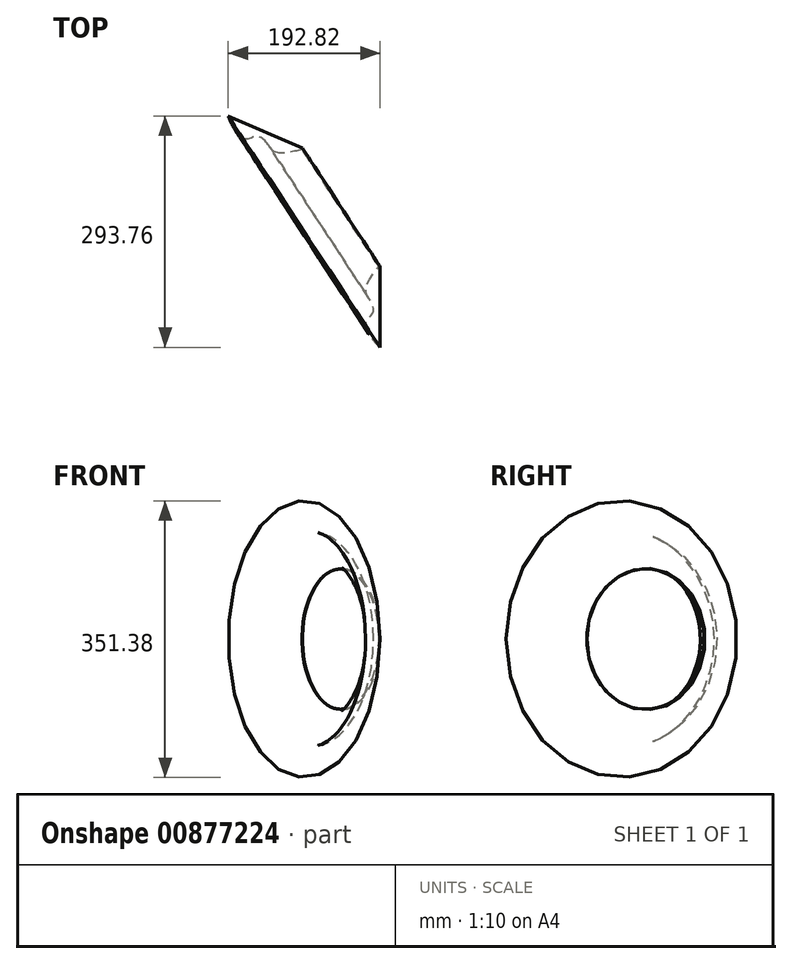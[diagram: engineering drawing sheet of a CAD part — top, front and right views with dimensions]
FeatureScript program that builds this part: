
annotation { "Feature Type Name" : "Feature", "Feature Type Description" : "" }
export const myFeature = defineFeature(function(context is Context, id is Id, definition is map)
    precondition{}
    {
        {
            var Q0;
            Q0=qCreatedBy(makeId("Top.planeOp"),FACE);
            var sketch = newSketch(context, id + "F0", { "sketchPlane" : qUnion([Q0])});
            skLineSegment(sketch, "E0.bottom", {"start": v(32.85, -53.53) * mm, "end": v(-32.85, -53.53) * mm});
            skLineSegment(sketch, "E0.top", {"start": v(32.85, 53.53) * mm, "end": v(-32.85, 53.53) * mm});
            skLineSegment(sketch, "E0.left", {"start": v(32.85, -53.53) * mm, "end": v(32.85, 53.53) * mm});
            skLineSegment(sketch, "E0.right", {"start": v(-32.85, -53.53) * mm, "end": v(-32.85, 53.53) * mm});
            skPoint(sketch, "E0.middle", {"position": v(0, 0) * mm});
            skLineSegment(sketch, "E1", {"start": v(-61.74, 98.82) * mm, "end": v(0, 139.34) * mm, "construction": true});
            skFitSpline(sketch, "E2", {"points": [v(37.08, -53.53) * mm, v(23.2, -6.68) * mm, v(20.56, 10.26) * mm, v(31.99, 54.19) * mm], "startDerivative": vector(-284.34, 280.53) * mm, "endDerivative": vector(200.4, 238.82) * mm});
            skSolve(sketch);
        }
        {
            var Q0;
            {var subQ2=sQuery(id+"F0.wireOp",EDGE,"E0.top");Q0=makeQuery(id+"F0.imprint","IMPRINT",FACE,{"disambiguationData":[TD([[makeQuery(id+"F0.imprint","IMPRINT",EDGE,{"derivedFrom":subQ2}),1.0]])]});}
            var Q1;
            Q1=sQuery(id+"F0.wireOp",EDGE,"E1");
            revolve(context, id + "F1", {"surfaceOperationType" : NewSurfaceOperationType.NEW, "entities" : qUnion([Q0]), "axis" : qUnion([Q1]), "revolveType" : RevolveType.FULL});
        }
    });
